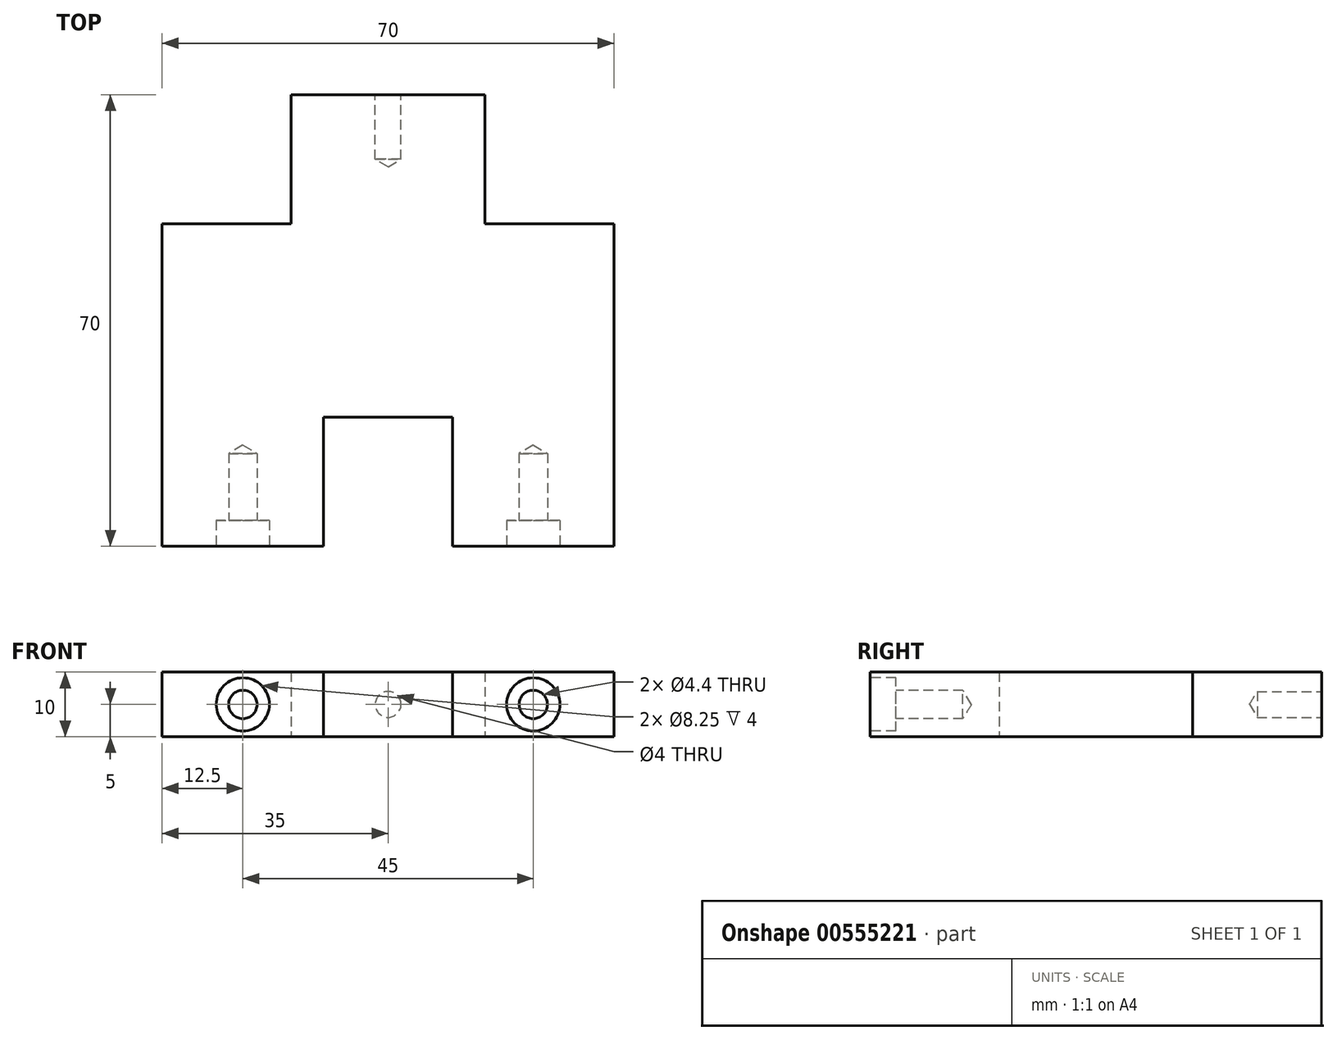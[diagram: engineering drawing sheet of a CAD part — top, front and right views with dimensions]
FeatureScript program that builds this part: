
annotation { "Feature Type Name" : "Feature", "Feature Type Description" : "" }
export const myFeature = defineFeature(function(context is Context, id is Id, definition is map)
    precondition{}
    {
        {
            var Q0;
            Q0=qCreatedBy(makeId("Top.planeOp"),FACE);
            var sketch = newSketch(context, id + "F0", { "sketchPlane" : qUnion([Q0])});
            skLineSegment(sketch, "E0.bottom", {"start": v(-35, 50) * mm, "end": v(35, 50) * mm});
            skLineSegment(sketch, "E0.top", {"start": v(-35, 0) * mm, "end": v(35, 0) * mm});
            skLineSegment(sketch, "E0.left", {"start": v(-35, 50) * mm, "end": v(-35, 0) * mm});
            skLineSegment(sketch, "E0.right", {"start": v(35, 50) * mm, "end": v(35, 0) * mm});
            skLineSegment(sketch, "E1.bottom", {"start": v(-10, 20) * mm, "end": v(10, 20) * mm});
            skLineSegment(sketch, "E1.top", {"start": v(-10, 0) * mm, "end": v(10, 0) * mm});
            skLineSegment(sketch, "E1.left", {"start": v(-10, 20) * mm, "end": v(-10, 0) * mm});
            skLineSegment(sketch, "E1.right", {"start": v(10, 20) * mm, "end": v(10, 0) * mm});
            skLineSegment(sketch, "E2.bottom", {"start": v(-15, 70) * mm, "end": v(15, 70) * mm});
            skLineSegment(sketch, "E2.top", {"start": v(-15, 50) * mm, "end": v(15, 50) * mm});
            skLineSegment(sketch, "E2.left", {"start": v(-15, 70) * mm, "end": v(-15, 50) * mm});
            skLineSegment(sketch, "E2.right", {"start": v(15, 70) * mm, "end": v(15, 50) * mm});
            skPoint(sketch, "E3", {"position": v(0, 50) * mm});
            skSolve(sketch);
        }
        {
            var Q0;
            {var subQ4=sQuery(id+"F0.wireOp",EDGE,"E0.left");Q0=makeQuery(id+"F0.imprint","IMPRINT",FACE,{"disambiguationData":[TD([[makeQuery(id+"F0.imprint","IMPRINT",EDGE,{"derivedFrom":subQ4}),1.0]])]});}
            var Q1;
            Q1=makeQuery(id+"F0.imprint","IMPRINT",FACE,{"disambiguationData":[TD([[makeQuery(id+"F0.imprint","IMPRINT",EDGE,{"derivedFrom":sQuery(id+"F0.wireOp",EDGE,"E2.bottom")}),-1.0]])]});
            extrude(context, id + "F1", {"entities" : qUnion([Q0, Q1]), "depth" : 10 * mm, "offsetDistance" : 25 * mm});
        }
        {
            var Q0;
            {var subQ0=sQuery(id+"F0.wireOp",EDGE,"E0.top");Q0=makeQuery(id+"F1.opExtrude","SWEPT_FACE",FACE,{"disambiguationData":[OSD([subQ0]),TDD([makeQuery(id+"F0.imprint","IMPRINT",EDGE,{"disambiguationData":[TD([[makeQuery(id+"F0.imprint","INTERSECT",VERTEX,{"derivedFrom":[subQ0,sQuery(id+"F0.wireOp",EDGE,"E0.left")]}),-1.0]])],"derivedFrom":subQ0})])]});}
            var sketch = newSketch(context, id + "F2", { "sketchPlane" : qUnion([Q0])});
            skPoint(sketch, "E4", {"position": v(-22.5, 5) * mm});
            skPoint(sketch, "E4.positionSnap0", {"position": v(-35, 5) * mm});
            skPoint(sketch, "E4.positionSnap1", {"position": v(-22.5, 0) * mm});
            skSolve(sketch);
        }
        {
            var Q0;
            {var subQ0=sQuery(id+"F0.wireOp",EDGE,"E0.top");Q0=makeQuery(id+"F1.opExtrude","SWEPT_FACE",FACE,{"disambiguationData":[OSD([subQ0]),TDD([makeQuery(id+"F0.imprint","IMPRINT",EDGE,{"disambiguationData":[TD([[makeQuery(id+"F0.imprint","INTERSECT",VERTEX,{"derivedFrom":[subQ0,sQuery(id+"F0.wireOp",EDGE,"E0.right")]}),1.0]])],"derivedFrom":subQ0})])]});}
            var sketch = newSketch(context, id + "F3", { "sketchPlane" : qUnion([Q0])});
            skPoint(sketch, "E5", {"position": v(22.5, 5) * mm});
            skPoint(sketch, "E5.positionSnap0", {"position": v(10, 5) * mm});
            skPoint(sketch, "E5.positionSnap1", {"position": v(22.5, 0) * mm});
            skSolve(sketch);
        }
        {
            var Q0;
            Q0=sQuery(id+"F2.wireOp",VERTEX,"E4");
            var Q1;
            Q1=sQuery(id+"F3.wireOp",VERTEX,"E5");
            var Q2;
            Q2=makeQuery(id+"F1.opExtrude","SWEPT_BODY",BODY,{"disambiguationData":[OSD([sQuery(id+"F0.wireOp",EDGE,"E0.bottom"),sQuery(id+"F0.wireOp",EDGE,"E0.top"),sQuery(id+"F0.wireOp",EDGE,"E0.left"),sQuery(id+"F0.wireOp",EDGE,"E0.right"),sQuery(id+"F0.wireOp",EDGE,"E1.bottom"),sQuery(id+"F0.wireOp",EDGE,"E1.left"),sQuery(id+"F0.wireOp",EDGE,"E1.right"),sQuery(id+"F0.wireOp",EDGE,"E2.bottom"),sQuery(id+"F0.wireOp",EDGE,"E2.left"),sQuery(id+"F0.wireOp",EDGE,"E2.right")])]});
            hole(context, id + "F4", {"style" : HoleStyle.C_BORE, "endStyle" : HoleEndStyle.BLIND, "standardTappedOrClearance" : lookupTablePath({ "standard" : "ISO", "fit" : "Normal", "size" : "M4", "type" : "Clearance" }), "standardBlindInLast" : lookupTablePath({ "fit" : "Standard", "standard" : "ISO", "size" : "M4", "type" : "Clearance" }), "holeDiameter" : 4.4 * mm, "cBoreDiameter" : 8.25 * mm, "cBoreDepth" : 4 * mm, "holeDepth" : 14.4 * mm, "isTappedThrough" : true, "tappedDepth" : 12 * mm, "tapClearance" : 3, "startFromSketch" : true, "locations" : qUnion([Q0, Q1]), "scope" : qUnion([Q2])});
        }
        {
            var Q0;
            Q0=makeQuery(id+"F1.opExtrude","SWEPT_FACE",FACE,{"disambiguationData":[OSD([sQuery(id+"F0.wireOp",EDGE,"E2.bottom")])]});
            var sketch = newSketch(context, id + "F5", { "sketchPlane" : qUnion([Q0])});
            skPoint(sketch, "E6", {"position": v(0, 5) * mm});
            skPoint(sketch, "E6.positionSnap0", {"position": v(-15, 5) * mm});
            skSolve(sketch);
        }
        {
            var Q0;
            Q0=sQuery(id+"F5.wireOp",VERTEX,"E6");
            var Q1;
            Q1=makeQuery(id+"F1.opExtrude","SWEPT_BODY",BODY,{"disambiguationData":[OSD([sQuery(id+"F0.wireOp",EDGE,"E0.bottom"),sQuery(id+"F0.wireOp",EDGE,"E0.top"),sQuery(id+"F0.wireOp",EDGE,"E0.left"),sQuery(id+"F0.wireOp",EDGE,"E0.right"),sQuery(id+"F0.wireOp",EDGE,"E1.bottom"),sQuery(id+"F0.wireOp",EDGE,"E1.left"),sQuery(id+"F0.wireOp",EDGE,"E1.right"),sQuery(id+"F0.wireOp",EDGE,"E2.bottom"),sQuery(id+"F0.wireOp",EDGE,"E2.left"),sQuery(id+"F0.wireOp",EDGE,"E2.right")])]});
            hole(context, id + "F6", {"style" : HoleStyle.SIMPLE, "endStyle" : HoleEndStyle.BLIND, "holeDiameter" : 4 * mm, "holeDepth" : 10 * mm, "isTappedThrough" : true, "tappedDepth" : 12 * mm, "tapClearance" : 3, "startFromSketch" : true, "locations" : qUnion([Q0]), "scope" : qUnion([Q1])});
        }
    });
